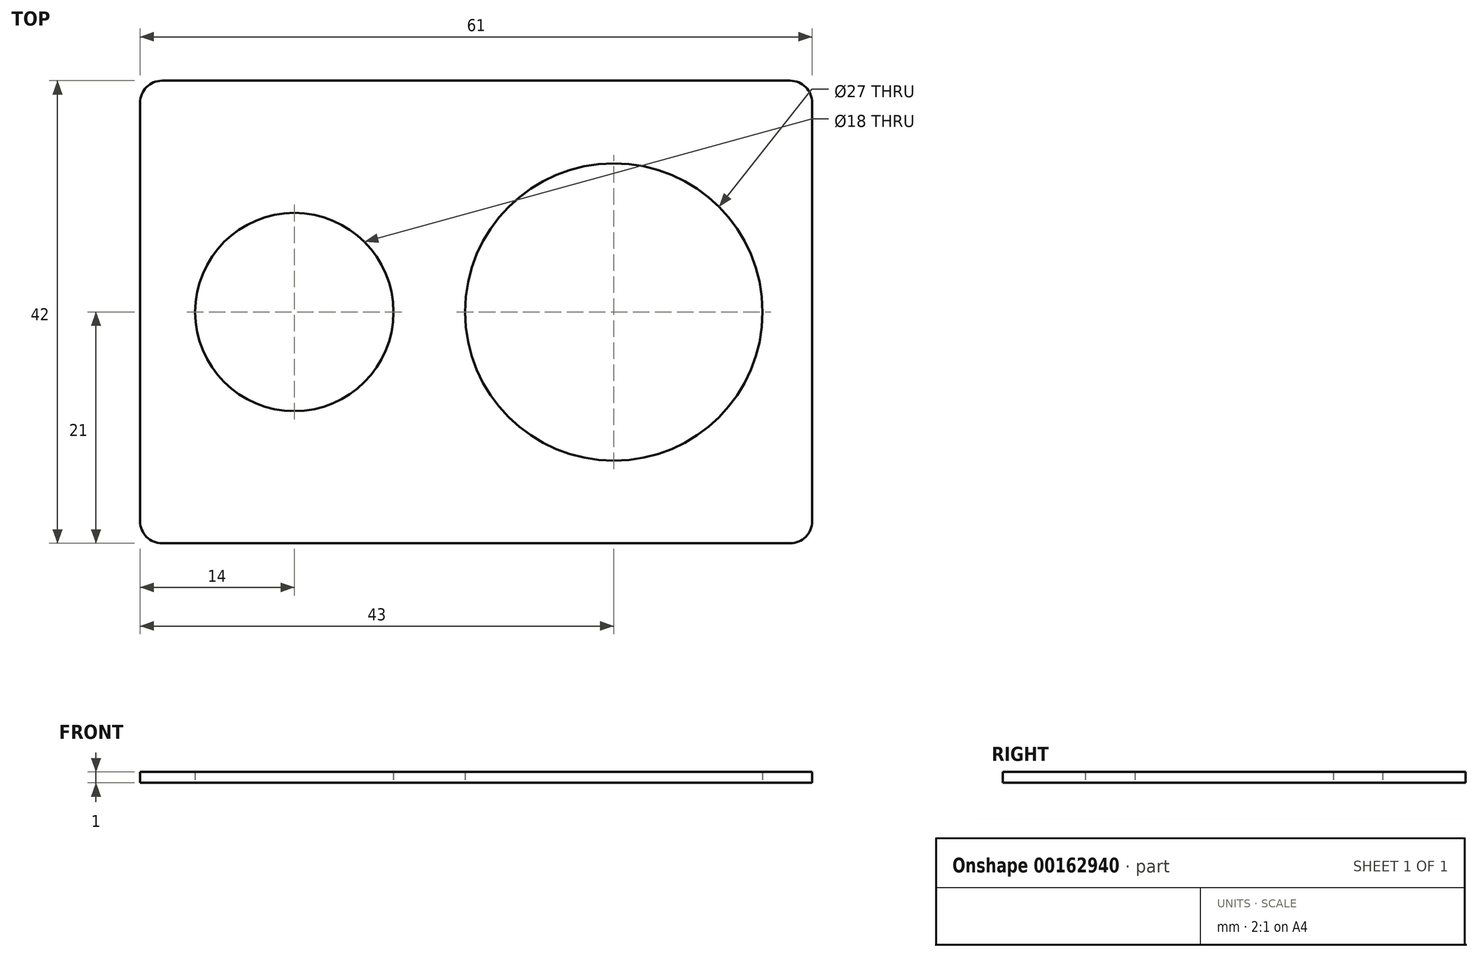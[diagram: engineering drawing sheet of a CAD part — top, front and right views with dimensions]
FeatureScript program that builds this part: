
annotation { "Feature Type Name" : "Feature", "Feature Type Description" : "" }
export const myFeature = defineFeature(function(context is Context, id is Id, definition is map)
    precondition{}
    {
        {
            var Q0;
            Q0=qCreatedBy(makeId("Top.planeOp"),FACE);
            var sketch = newSketch(context, id + "F0", { "sketchPlane" : qUnion([Q0])});
            skLineSegment(sketch, "E0.bottom", {"start": v(-30.5, 21) * mm, "end": v(30.5, 21) * mm});
            skLineSegment(sketch, "E0.top", {"start": v(-30.5, -21) * mm, "end": v(30.5, -21) * mm});
            skLineSegment(sketch, "E0.left", {"start": v(-30.5, 21) * mm, "end": v(-30.5, -21) * mm});
            skLineSegment(sketch, "E0.right", {"start": v(30.5, 21) * mm, "end": v(30.5, -21) * mm});
            skPoint(sketch, "E0.middle", {"position": v(0, 0) * mm});
            skCircle(sketch, "E1", {"center": v(12.5, 0) * mm, "radius": 13.5 * mm});
            skCircle(sketch, "E2", {"center": v(-16.5, 0) * mm, "radius": 9 * mm});
            skSolve(sketch);
        }
        {
            var Q0;
            Q0=makeQuery(id+"F0.imprint","IMPRINT",FACE,{"disambiguationData":[TD([[makeQuery(id+"F0.imprint","IMPRINT",EDGE,{"derivedFrom":sQuery(id+"F0.wireOp",EDGE,"E0.bottom")}),-1.0]])]});
            extrude(context, id + "F1", {"entities" : qUnion([Q0]), "depth" : 1 * mm});
        }
        {
            var Q0;
            Q0=makeQuery(id+"F1.opExtrude","SWEPT_EDGE",EDGE,{"disambiguationData":[OSD([sQuery(id+"F0.wireOp",EDGE,"E0.bottom"),sQuery(id+"F0.wireOp",EDGE,"E0.left")])]});
            var Q1;
            Q1=makeQuery(id+"F1.opExtrude","SWEPT_EDGE",EDGE,{"disambiguationData":[OSD([sQuery(id+"F0.wireOp",EDGE,"E0.bottom"),sQuery(id+"F0.wireOp",EDGE,"E0.right")])]});
            var Q2;
            Q2=makeQuery(id+"F1.opExtrude","SWEPT_EDGE",EDGE,{"disambiguationData":[OSD([sQuery(id+"F0.wireOp",EDGE,"E0.top"),sQuery(id+"F0.wireOp",EDGE,"E0.right")])]});
            var Q3;
            Q3=makeQuery(id+"F1.opExtrude","SWEPT_EDGE",EDGE,{"disambiguationData":[OSD([sQuery(id+"F0.wireOp",EDGE,"E0.top"),sQuery(id+"F0.wireOp",EDGE,"E0.left")])]});
            fillet(context, id + "F2", {"entities" : qUnion([Q0, Q1, Q2, Q3]), "radius" : 2 * mm, "tangentPropagation" : true, "allowEdgeOverflow" : false});
        }
    });
